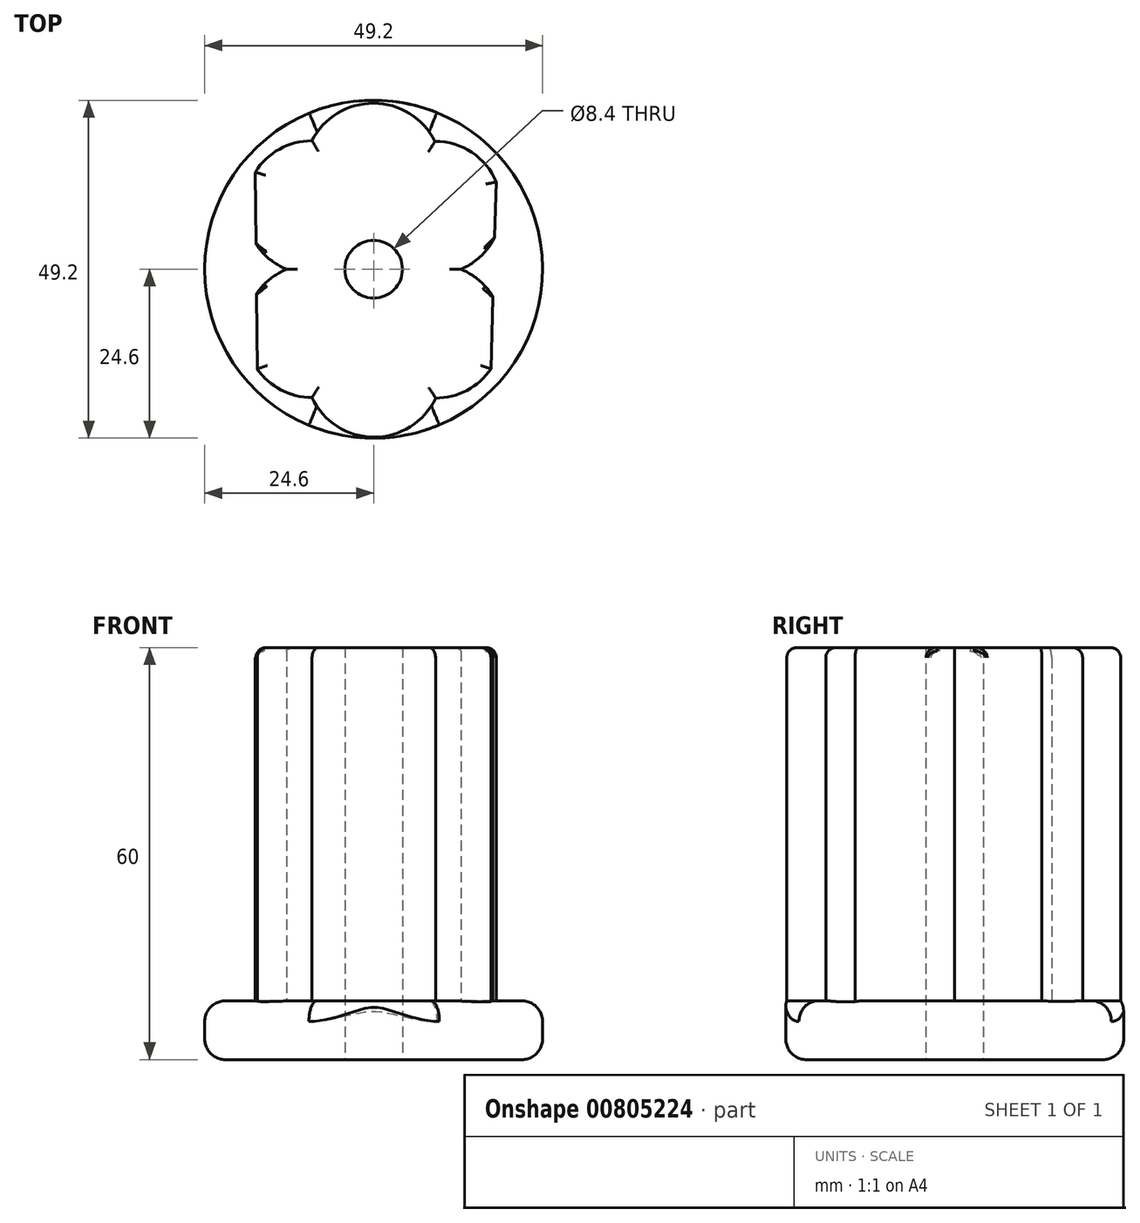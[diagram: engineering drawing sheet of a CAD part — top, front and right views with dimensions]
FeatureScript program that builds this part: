
annotation { "Feature Type Name" : "Feature", "Feature Type Description" : "" }
export const myFeature = defineFeature(function(context is Context, id is Id, definition is map)
    precondition{}
    {
        {
            var Q0;
            Q0=qCreatedBy(makeId("Top.planeOp"),FACE);
            var sketch = newSketch(context, id + "F0", { "sketchPlane" : qUnion([Q0])});
            skCircle(sketch, "E0", {"center": v(0, 0) * mm, "radius": 4.2 * mm});
            skCircle(sketch, "E1", {"center": v(0, 0) * mm, "radius": 12.7 * mm});
            skArc(sketch, "E2", {"start": v(12.7, 0) * mm, "mid": v(15.6, 1.88) * mm, "end": v(17.64, 4.66) * mm});
            skArc(sketch, "E3", {"start": v(-12.7, 0) * mm, "mid": v(-15.15, -1.47) * mm, "end": v(-17.07, -3.6) * mm});
            skArc(sketch, "E4", {"start": v(0, 12.7) * mm, "mid": v(-8.19, 18.68) * mm, "end": v(-17.24, 14.13) * mm});
            skArc(sketch, "E5", {"start": v(0, -12.7) * mm, "mid": v(8, -18.72) * mm, "end": v(17.08, -14.51) * mm});
            skArc(sketch, "E6", {"start": v(8.94, 18.63) * mm, "mid": v(0, 24.18) * mm, "end": v(-8.99, 18.71) * mm});
            skArc(sketch, "E7", {"start": v(-8.97, -18.7) * mm, "mid": v(0, -24.45) * mm, "end": v(9.03, -18.77) * mm});
            skLineSegment(sketch, "E8", {"start": v(17.87, 12.7) * mm, "end": v(17.64, 4.66) * mm});
            skLineSegment(sketch, "E9", {"start": v(-17.24, 14.13) * mm, "end": v(-17.14, 3.68) * mm});
            skArc(sketch, "E10.trimOffspring", {"start": v(-17.14, 3.68) * mm, "mid": v(-15.2, 1.5) * mm, "end": v(-12.7, 0) * mm});
            skArc(sketch, "E11.trimOffspring", {"start": v(-16.96, -14.51) * mm, "mid": v(-7.94, -18.64) * mm, "end": v(0, -12.7) * mm});
            skArc(sketch, "E12.trimOffspring", {"start": v(17.39, -4.02) * mm, "mid": v(15.37, -1.63) * mm, "end": v(12.7, 0) * mm});
            skArc(sketch, "E13.trimOffspring", {"start": v(17.87, 12.7) * mm, "mid": v(8.94, 18.63) * mm, "end": v(0, 12.7) * mm});
            skLineSegment(sketch, "E14.trimOffspring", {"start": v(-17.07, -3.6) * mm, "end": v(-16.96, -14.51) * mm});
            skLineSegment(sketch, "E15.trimOffspring", {"start": v(17.39, -4.02) * mm, "end": v(17.08, -14.51) * mm});
            skSolve(sketch);
        }
        {
            var Q0;
            {var subQ3=sQuery(id+"F0.wireOp",EDGE,"E2");Q0=makeQuery(id+"F0.imprint","IMPRINT",FACE,{"disambiguationData":[TD([[makeQuery(id+"F0.imprint","IMPRINT",EDGE,{"derivedFrom":subQ3}),1.0]])]});}
            var Q1;
            {var subQ0=sQuery(id+"F0.wireOp",EDGE,"E9");Q1=makeQuery(id+"F0.imprint","IMPRINT",FACE,{"disambiguationData":[TD([[makeQuery(id+"F0.imprint","IMPRINT",EDGE,{"derivedFrom":subQ0}),1.0]])]});}
            var Q2;
            {var subQ4=sQuery(id+"F0.wireOp",EDGE,"E3");Q2=makeQuery(id+"F0.imprint","IMPRINT",FACE,{"disambiguationData":[TD([[makeQuery(id+"F0.imprint","IMPRINT",EDGE,{"derivedFrom":subQ4}),1.0]])]});}
            var Q3;
            {var subQ3=sQuery(id+"F0.wireOp",EDGE,"E6");Q3=makeQuery(id+"F0.imprint","IMPRINT",FACE,{"disambiguationData":[TD([[makeQuery(id+"F0.imprint","IMPRINT",EDGE,{"derivedFrom":subQ3}),1.0]])]});}
            var Q4;
            {var subQ3=sQuery(id+"F0.wireOp",EDGE,"E7");Q4=makeQuery(id+"F0.imprint","IMPRINT",FACE,{"disambiguationData":[TD([[makeQuery(id+"F0.imprint","IMPRINT",EDGE,{"derivedFrom":subQ3}),1.0]])]});}
            var Q5;
            Q5=makeQuery(id+"F0.imprint","IMPRINT",FACE,{"disambiguationData":[TD([[makeQuery(id+"F0.imprint","IMPRINT",EDGE,{"derivedFrom":sQuery(id+"F0.wireOp",EDGE,"E0")}),-1.0]])]});
            var Q6;
            {var subQ0=sQuery(id+"F0.wireOp",EDGE,"E12.trimOffspring");Q6=makeQuery(id+"F0.imprint","IMPRINT",FACE,{"disambiguationData":[TD([[makeQuery(id+"F0.imprint","IMPRINT",EDGE,{"derivedFrom":subQ0}),1.0]])]});}
            extrude(context, id + "F1", {"entities" : qUnion([Q0, Q1, Q2, Q3, Q4, Q5, Q6]), "depth" : 60 * mm, "offsetDistance" : 25 * mm});
        }
        {
            var Q0;
            Q0=makeQuery(id+"F1.opExtrude","CAP_EDGE",EDGE,{"disambiguationData":[OSD([sQuery(id+"F0.wireOp",EDGE,"E6")])],"isStart":false});
            var Q1;
            Q1=makeQuery(id+"F1.opExtrude","CAP_EDGE",EDGE,{"disambiguationData":[OSD([sQuery(id+"F0.wireOp",EDGE,"E4")])],"isStart":false});
            var Q2;
            Q2=makeQuery(id+"F1.opExtrude","CAP_EDGE",EDGE,{"disambiguationData":[OSD([sQuery(id+"F0.wireOp",EDGE,"E9")])],"isStart":false});
            var Q3;
            Q3=makeQuery(id+"F1.opExtrude","CAP_EDGE",EDGE,{"disambiguationData":[OSD([sQuery(id+"F0.wireOp",EDGE,"E14.trimOffspring")])],"isStart":false});
            var Q4;
            Q4=makeQuery(id+"F1.opExtrude","CAP_EDGE",EDGE,{"disambiguationData":[OSD([sQuery(id+"F0.wireOp",EDGE,"E11.trimOffspring")])],"isStart":false});
            var Q5;
            Q5=makeQuery(id+"F1.opExtrude","CAP_EDGE",EDGE,{"disambiguationData":[OSD([sQuery(id+"F0.wireOp",EDGE,"E7")])],"isStart":false});
            var Q6;
            Q6=makeQuery(id+"F1.opExtrude","CAP_EDGE",EDGE,{"disambiguationData":[OSD([sQuery(id+"F0.wireOp",EDGE,"E5")])],"isStart":false});
            var Q7;
            Q7=makeQuery(id+"F1.opExtrude","CAP_EDGE",EDGE,{"disambiguationData":[OSD([sQuery(id+"F0.wireOp",EDGE,"E15.trimOffspring")])],"isStart":false});
            var Q8;
            Q8=makeQuery(id+"F1.opExtrude","CAP_EDGE",EDGE,{"disambiguationData":[OSD([sQuery(id+"F0.wireOp",EDGE,"E8")])],"isStart":false});
            var Q9;
            Q9=makeQuery(id+"F1.opExtrude","CAP_EDGE",EDGE,{"disambiguationData":[OSD([sQuery(id+"F0.wireOp",EDGE,"E13.trimOffspring")])],"isStart":false});
            fillet(context, id + "F2", {"entities" : qUnion([Q0, Q1, Q2, Q3, Q4, Q5, Q6, Q7, Q8, Q9]), "radius" : 1.5 * mm, "tangentPropagation" : true, "allowEdgeOverflow" : false});
        }
        {
            var Q0;
            Q0=makeQuery(id+"F1.opExtrude","CAP_EDGE",EDGE,{"disambiguationData":[OSD([sQuery(id+"F0.wireOp",EDGE,"E7")])],"isStart":true});
            var Q1;
            Q1=makeQuery(id+"F1.opExtrude","CAP_EDGE",EDGE,{"disambiguationData":[OSD([sQuery(id+"F0.wireOp",EDGE,"E11.trimOffspring")])],"isStart":true});
            var Q2;
            Q2=makeQuery(id+"F1.opExtrude","CAP_EDGE",EDGE,{"disambiguationData":[OSD([sQuery(id+"F0.wireOp",EDGE,"E14.trimOffspring")])],"isStart":true});
            var Q3;
            Q3=makeQuery(id+"F1.opExtrude","CAP_EDGE",EDGE,{"disambiguationData":[OSD([sQuery(id+"F0.wireOp",EDGE,"E9")])],"isStart":true});
            var Q4;
            Q4=makeQuery(id+"F1.opExtrude","CAP_EDGE",EDGE,{"disambiguationData":[OSD([sQuery(id+"F0.wireOp",EDGE,"E4")])],"isStart":true});
            var Q5;
            Q5=makeQuery(id+"F1.opExtrude","CAP_EDGE",EDGE,{"disambiguationData":[OSD([sQuery(id+"F0.wireOp",EDGE,"E6")])],"isStart":true});
            var Q6;
            Q6=makeQuery(id+"F1.opExtrude","CAP_EDGE",EDGE,{"disambiguationData":[OSD([sQuery(id+"F0.wireOp",EDGE,"E13.trimOffspring")])],"isStart":true});
            var Q7;
            Q7=makeQuery(id+"F1.opExtrude","CAP_EDGE",EDGE,{"disambiguationData":[OSD([sQuery(id+"F0.wireOp",EDGE,"E8")])],"isStart":true});
            var Q8;
            Q8=makeQuery(id+"F1.opExtrude","CAP_EDGE",EDGE,{"disambiguationData":[OSD([sQuery(id+"F0.wireOp",EDGE,"E15.trimOffspring")])],"isStart":true});
            var Q9;
            Q9=makeQuery(id+"F1.opExtrude","CAP_EDGE",EDGE,{"disambiguationData":[OSD([sQuery(id+"F0.wireOp",EDGE,"E5")])],"isStart":true});
            fillet(context, id + "F3", {"entities" : qUnion([Q0, Q1, Q2, Q3, Q4, Q5, Q6, Q7, Q8, Q9]), "radius" : 1.5 * mm, "tangentPropagation" : true, "allowEdgeOverflow" : false});
        }
        {
            var Q0;
            Q0=makeQuery(id+"F1.opExtrude","CAP_EDGE",EDGE,{"disambiguationData":[OSD([sQuery(id+"F0.wireOp",EDGE,"E3")])],"isStart":true});
            var Q1;
            Q1=makeQuery(id+"F1.opExtrude","CAP_EDGE",EDGE,{"disambiguationData":[OSD([sQuery(id+"F0.wireOp",EDGE,"E10.trimOffspring")])],"isStart":true});
            var Q2;
            Q2=makeQuery(id+"F1.opExtrude","CAP_EDGE",EDGE,{"disambiguationData":[OSD([sQuery(id+"F0.wireOp",EDGE,"E12.trimOffspring")])],"isStart":true});
            var Q3;
            Q3=makeQuery(id+"F1.opExtrude","CAP_EDGE",EDGE,{"disambiguationData":[OSD([sQuery(id+"F0.wireOp",EDGE,"E2")])],"isStart":true});
            fillet(context, id + "F4", {"entities" : qUnion([Q0, Q1, Q2, Q3]), "radius" : .5 * mm, "tangentPropagation" : true, "allowEdgeOverflow" : false});
        }
        {
            var Q0;
            Q0=qCreatedBy(makeId("Top.planeOp"),FACE);
            var sketch = newSketch(context, id + "F5", { "sketchPlane" : qUnion([Q0])});
            skCircle(sketch, "E16", {"center": v(0, 0) * mm, "radius": 24.6 * mm});
            skCircle(sketch, "E17", {"center": v(0, 0) * mm, "radius": 4.2 * mm});
            skSolve(sketch);
        }
        {
            var Q0;
            Q0=makeQuery(id+"F5.imprint","IMPRINT",FACE,{"disambiguationData":[TD([[makeQuery(id+"F5.imprint","IMPRINT",EDGE,{"derivedFrom":sQuery(id+"F5.wireOp",EDGE,"E16")}),1.0]])]});
            extrude(context, id + "F6", {"entities" : qUnion([Q0]), "operationType" : NewBodyOperationType.ADD, "depth" : 8.56 * mm, "offsetDistance" : 25 * mm});
        }
        {
            var Q0;
            Q0=makeQuery(id+"F6.opExtrude","CAP_EDGE",EDGE,{"disambiguationData":[OSD([sQuery(id+"F5.wireOp",EDGE,"E16")])],"isStart":false});
            fillet(context, id + "F7", {"entities" : qUnion([Q0]), "radius" : 3 * mm, "tangentPropagation" : true, "allowEdgeOverflow" : false});
        }
        {
            var Q0;
            Q0=makeQuery(id+"F6.opExtrude","CAP_EDGE",EDGE,{"disambiguationData":[OSD([sQuery(id+"F5.wireOp",EDGE,"E16")])],"isStart":true});
            fillet(context, id + "F8", {"entities" : qUnion([Q0]), "radius" : 3 * mm, "tangentPropagation" : true, "allowEdgeOverflow" : false});
        }
    });
